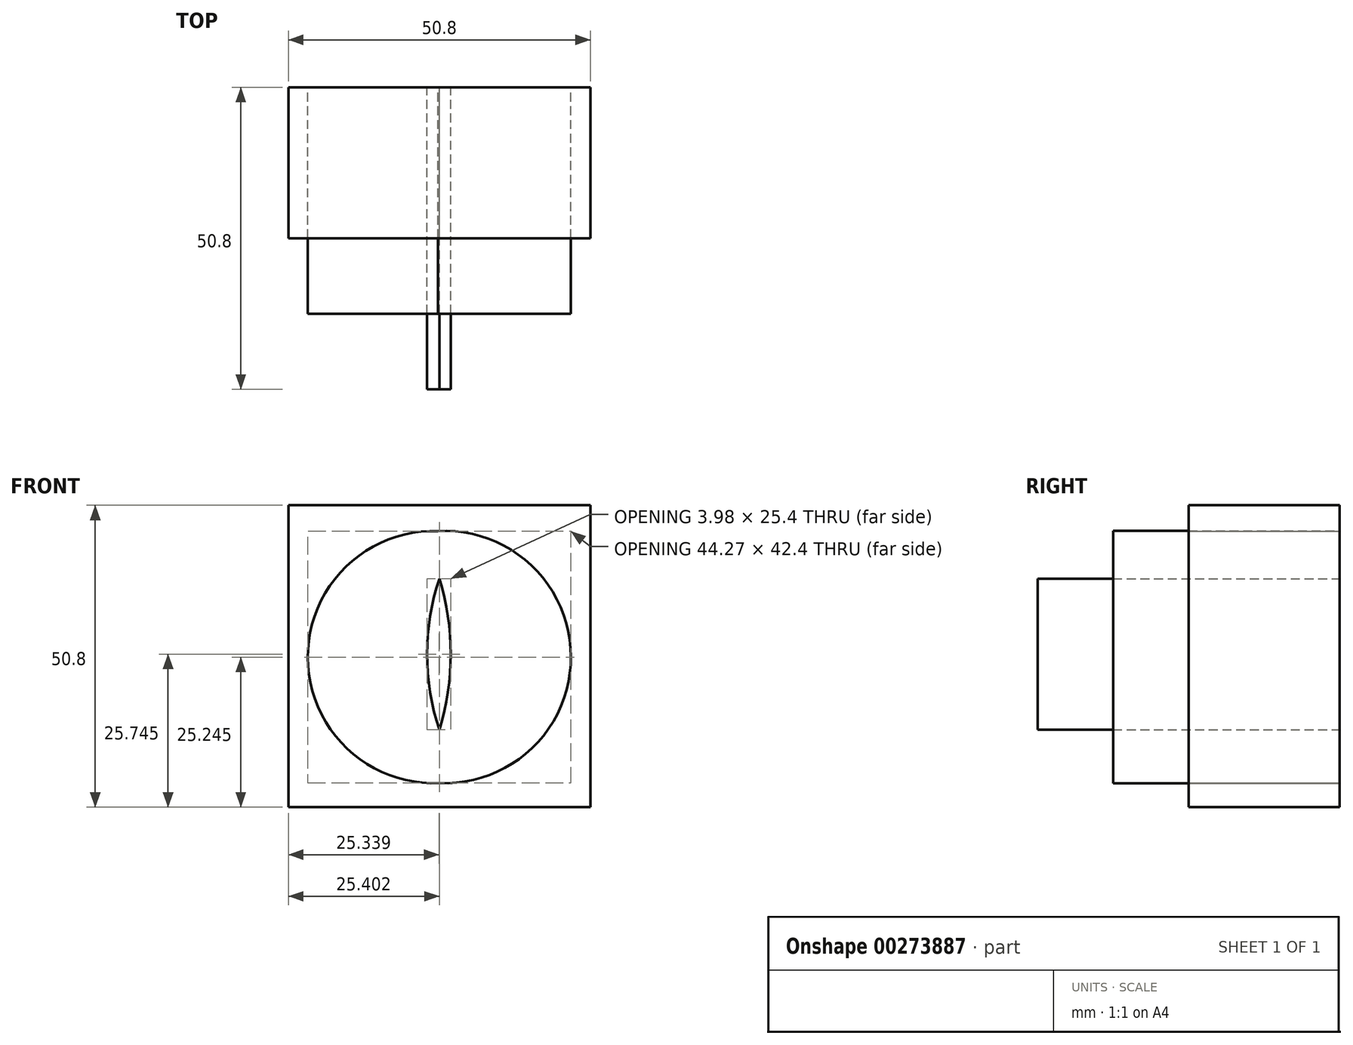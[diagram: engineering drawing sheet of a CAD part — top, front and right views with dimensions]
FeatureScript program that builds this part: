
annotation { "Feature Type Name" : "Feature", "Feature Type Description" : "" }
export const myFeature = defineFeature(function(context is Context, id is Id, definition is map)
    precondition{}
    {
        {
            var Q0;
            Q0=qCreatedBy(makeId("Front.planeOp"),FACE);
            var sketch = newSketch(context, id + "F0", { "sketchPlane" : qUnion([Q0])});
            skLineSegment(sketch, "E0.bottom", {"start": v(-39.41, 43.78) * mm, "end": v(11.39, 43.78) * mm});
            skLineSegment(sketch, "E0.top", {"start": v(-39.41, -7.02) * mm, "end": v(11.39, -7.02) * mm});
            skLineSegment(sketch, "E0.left", {"start": v(-39.41, 43.78) * mm, "end": v(-39.41, -7.02) * mm});
            skLineSegment(sketch, "E0.right", {"start": v(11.39, 43.78) * mm, "end": v(11.39, -7.02) * mm});
            skArc(sketch, "E1", {"start": v(-14.01, 6.03) * mm, "mid": v(-12.08, 18.73) * mm, "end": v(-14.01, 31.43) * mm});
            skArc(sketch, "E2", {"start": v(-14.01, 31.43) * mm, "mid": v(-16.06, 18.73) * mm, "end": v(-14.01, 6.03) * mm});
            skArc(sketch, "E3", {"start": v(-14.22, 39.42) * mm, "mid": v(-36.14, 18.12) * mm, "end": v(-14.01, -2.97) * mm});
            skPoint(sketch, "E3.endSnap0", {"position": v(-14.01, -7.02) * mm});
            skArc(sketch, "E4", {"start": v(-14.01, -2.97) * mm, "mid": v(8.12, 18.33) * mm, "end": v(-14.22, 39.42) * mm});
            skSolve(sketch);
        }
        {
            var Q0;
            Q0=makeQuery(id+"F0.imprint","IMPRINT",FACE,{"disambiguationData":[TD([[makeQuery(id+"F0.imprint","IMPRINT",EDGE,{"derivedFrom":sQuery(id+"F0.wireOp",EDGE,"E0.bottom")}),-1.0]])]});
            extrude(context, id + "F1", {"entities" : qUnion([Q0]), "depth" : 25.4 * mm});
        }
        {
            var Q0;
            Q0=makeQuery(id+"F0.imprint","IMPRINT",FACE,{"disambiguationData":[TD([[makeQuery(id+"F0.imprint","IMPRINT",EDGE,{"derivedFrom":sQuery(id+"F0.wireOp",EDGE,"E1")}),1.0]])]});
            extrude(context, id + "F2", {"entities" : qUnion([Q0]), "depth" : 50.8 * mm});
        }
        {
            var Q0;
            Q0=makeQuery(id+"F0.imprint","IMPRINT",FACE,{"disambiguationData":[TD([[makeQuery(id+"F0.imprint","IMPRINT",EDGE,{"derivedFrom":sQuery(id+"F0.wireOp",EDGE,"E1")}),-1.0]])]});
            extrude(context, id + "F3", {"entities" : qUnion([Q0]), "depth" : 38.1 * mm});
        }
    });
